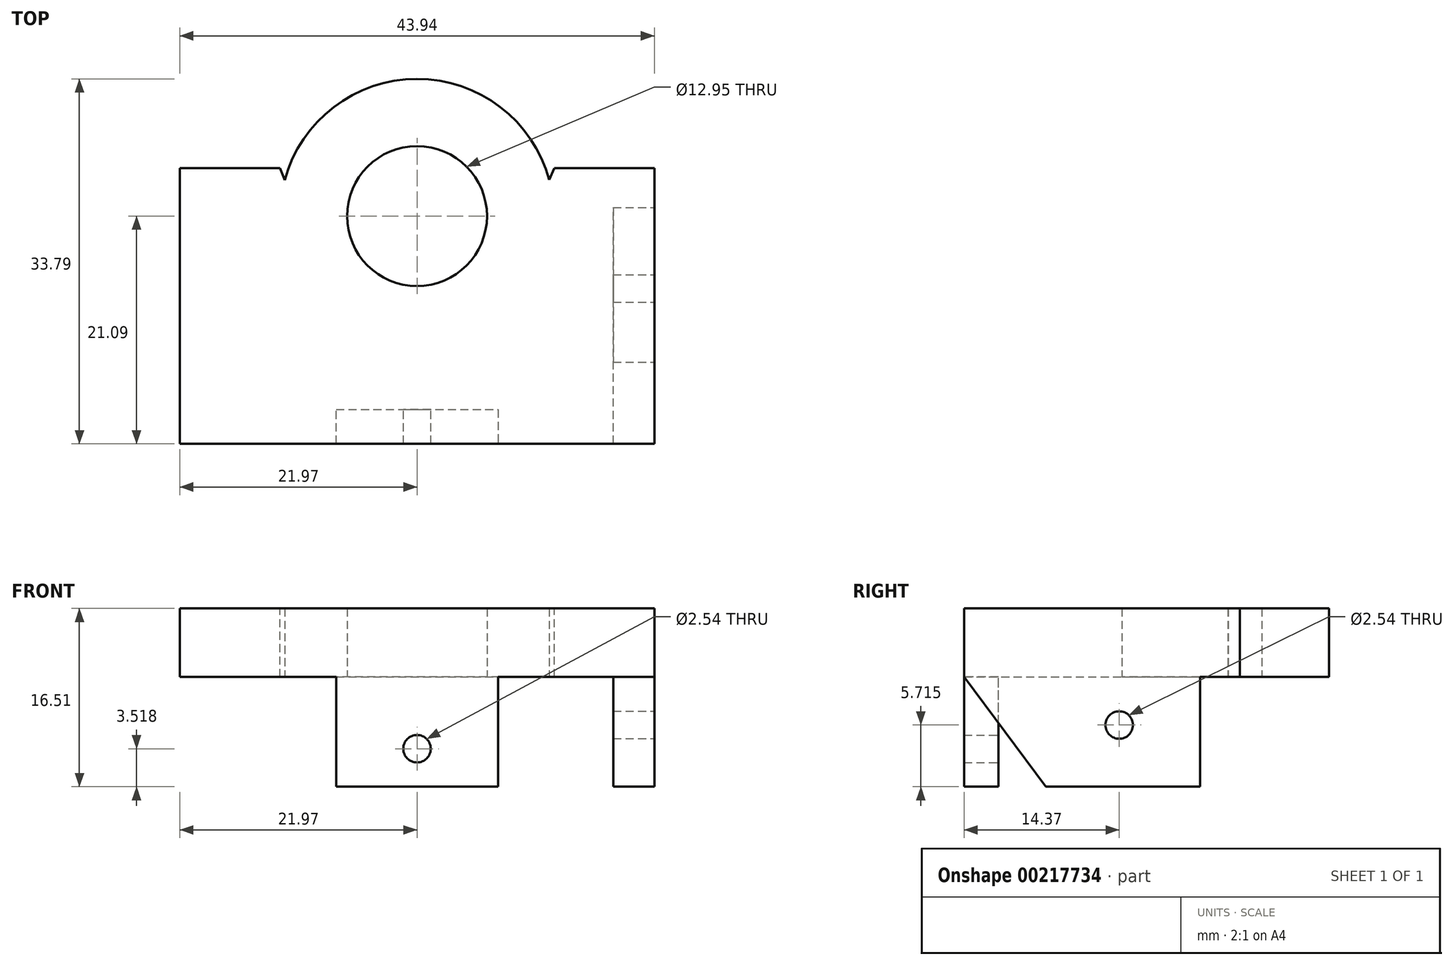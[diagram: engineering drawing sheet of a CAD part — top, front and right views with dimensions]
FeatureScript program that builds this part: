
annotation { "Feature Type Name" : "Feature", "Feature Type Description" : "" }
export const myFeature = defineFeature(function(context is Context, id is Id, definition is map)
    precondition{}
    {
        {
            var Q0;
            Q0=qCreatedBy(makeId("Top.planeOp"),FACE);
            var sketch = newSketch(context, id + "F0", { "sketchPlane" : qUnion([Q0])});
            skCircle(sketch, "E0", {"center": v(0, 0) * mm, "radius": 6.48 * mm});
            skCircle(sketch, "E1", {"center": v(0, 0) * mm, "radius": 12.7 * mm});
            skSolve(sketch);
        }
        {
            var Q0;
            Q0=qSketchRegion(id+"F0",true);
            extrude(context, id + "F1", {"entities" : qUnion([Q0]), "depth" : 6.35 * mm});
        }
        {
            var Q0;
            Q0=makeQuery(id+"F1.opExtrude","CAP_FACE",FACE,{"disambiguationData":[OSD([sQuery(id+"F0.wireOp",EDGE,"E0"),sQuery(id+"F0.wireOp",EDGE,"E1")])],"isStart":false});
            var sketch = newSketch(context, id + "F2", { "sketchPlane" : qUnion([Q0])});
            skLineSegment(sketch, "E2", {"start": v(0, -21.09) * mm, "end": v(-21.97, -21.09) * mm});
            skLineSegment(sketch, "E3", {"start": v(0, -21.09) * mm, "end": v(21.97, -21.09) * mm});
            skLineSegment(sketch, "E4", {"start": v(21.97, -21.09) * mm, "end": v(21.97, -17.91) * mm});
            skLineSegment(sketch, "E5", {"start": v(-21.97, -21.09) * mm, "end": v(-21.97, -17.9) * mm});
            skLineSegment(sketch, "E6", {"start": v(21.97, -17.91) * mm, "end": v(21.97, 4.45) * mm});
            skLineSegment(sketch, "E7", {"start": v(21.97, 4.45) * mm, "end": v(12.7, 4.45) * mm});
            skLineSegment(sketch, "E8", {"start": v(-21.97, -17.9) * mm, "end": v(-21.97, 4.45) * mm});
            skLineSegment(sketch, "E9", {"start": v(-21.97, 4.45) * mm, "end": v(-12.7, 4.45) * mm});
            skLineSegment(sketch, "E10", {"start": v(-12.7, 4.45) * mm, "end": v(-6.95, -9.77) * mm});
            skLineSegment(sketch, "E11", {"start": v(-6.95, -9.77) * mm, "end": v(6.77, -9.77) * mm});
            skLineSegment(sketch, "E12", {"start": v(6.77, -9.77) * mm, "end": v(12.7, 4.45) * mm});
            skSolve(sketch);
        }
        {
            var Q0;
            Q0=qSketchRegion(id+"F2",true);
            extrude(context, id + "F3", {"entities" : qUnion([Q0]), "operationType" : NewBodyOperationType.ADD, "oppositeDirection" : true, "depth" : 6.35 * mm});
        }
        {
            var Q0;
            Q0=makeQuery(id+"F3.opExtrude","SWEPT_FACE",FACE,{"disambiguationData":[OSD([sQuery(id+"F2.wireOp",EDGE,"E4")])]});
            var sketch = newSketch(context, id + "F4", { "sketchPlane" : qUnion([Q0])});
            skLineSegment(sketch, "E13", {"start": v(-21.09, 6.35) * mm, "end": v(0.78, 6.35) * mm});
            skLineSegment(sketch, "E14", {"start": v(0.78, 6.35) * mm, "end": v(0.78, -10.16) * mm});
            skLineSegment(sketch, "E15", {"start": v(0.78, -10.16) * mm, "end": v(-13.53, -10.16) * mm});
            skLineSegment(sketch, "E16", {"start": v(-21.09, 0) * mm, "end": v(-21.09, 6.35) * mm});
            skLineSegment(sketch, "E17", {"start": v(0.78, -10.16) * mm, "end": v(-6.72, -10.16) * mm});
            skLineSegment(sketch, "E18", {"start": v(-6.72, -10.16) * mm, "end": v(-6.72, -4.45) * mm});
            skPoint(sketch, "E18.endSnap0", {"position": v(0.78, -1.9) * mm});
            skCircle(sketch, "E19", {"center": v(-6.72, -4.45) * mm, "radius": 1.27 * mm});
            skLineSegment(sketch, "E20", {"start": v(-21.09, 0) * mm, "end": v(-13.53, -10.16) * mm});
            skPoint(sketch, "E21.orphan", {"position": v(-21.09, -10.16) * mm});
            skPoint(sketch, "E22.orphan", {"position": v(-6.72, -1.9) * mm});
            skSolve(sketch);
        }
        {
            var Q0;
            Q0 = qSketchRegion(id + "F4", true);
            extrude(context, id + "F5", {"entities" : qUnion([Q0]), "operationType" : NewBodyOperationType.ADD, "oppositeDirection" : true, "depth" : 3.8 * mm});
        }
        {
            var Q0;
            Q0=makeQuery(id+"F3.boolean.opBoolean","MERGE",FACE,{"derivedFrom":[makeQuery(id+"F1.opExtrude","CAP_FACE",FACE,{"disambiguationData":[OSD([sQuery(id+"F0.wireOp",EDGE,"E0"),sQuery(id+"F0.wireOp",EDGE,"E1")])],"isStart":true}),makeQuery(id+"F3.opExtrude","CAP_FACE",FACE,{"disambiguationData":[OSD([sQuery(id+"F2.wireOp",EDGE,"E2"),sQuery(id+"F2.wireOp",EDGE,"E3"),sQuery(id+"F2.wireOp",EDGE,"E4"),sQuery(id+"F2.wireOp",EDGE,"E5"),sQuery(id+"F2.wireOp",EDGE,"ihHadCWb-XjeW-R3a0-dGNE-DLv68DcTVQ7N"),sQuery(id+"F2.wireOp",EDGE,"1IoPUFMC-zjit-IGW3-BYE7-LK0CDHMM8rKh"),sQuery(id+"F2.wireOp",EDGE,"NdcEkIWE-Nxbb-I5WJ-c0X4-1hDUIVkZ8ckX"),sQuery(id+"F2.wireOp",EDGE,"YiZrzofx-tHcN-ggQp-RaR3-rrEU8t4WHX24"),sQuery(id+"F2.wireOp",EDGE,"RK1YeRvc-nPOg-Eqkx-etu6-UXfsHSOCRuCc"),sQuery(id+"F2.wireOp",EDGE,"3zleHhUL-0sEu-ddFR-184l-ClsJvtk2H4PM")])],"isStart":false})]});
            var sketch = newSketch(context, id + "F6", { "sketchPlane" : qUnion([Q0])});
            skLineSegment(sketch, "E23", {"start": v(0, 21.09) * mm, "end": v(7.5, 21.09) * mm});
            skLineSegment(sketch, "E24", {"start": v(0, 21.09) * mm, "end": v(-7.5, 21.09) * mm});
            skLineSegment(sketch, "E25", {"start": v(-7.5, 21.09) * mm, "end": v(-7.5, 17.91) * mm});
            skLineSegment(sketch, "E26", {"start": v(-7.5, 17.91) * mm, "end": v(7.5, 17.91) * mm});
            skLineSegment(sketch, "E27", {"start": v(7.5, 17.91) * mm, "end": v(7.5, 21.09) * mm});
            skSolve(sketch);
        }
        {
            var Q0;
            Q0 = qSketchRegion(id + "F6", true);
            extrude(context, id + "F7", {"entities" : qUnion([Q0]), "operationType" : NewBodyOperationType.ADD, "depth" : 10.16 * mm});
        }
        {
            var Q0;
            Q0=makeQuery(id+"F7.opExtrude","SWEPT_FACE",FACE,{"disambiguationData":[OSD([sQuery(id+"F6.wireOp",EDGE,"E26")])]});
            var sketch = newSketch(context, id + "F8", { "sketchPlane" : qUnion([Q0])});
            skLineSegment(sketch, "E28", {"start": v(0, -10.16) * mm, "end": v(0, -6.64) * mm});
            skPoint(sketch, "E28.endSnap0", {"position": v(0, -10.16) * mm});
            skCircle(sketch, "E29", {"center": v(0, -6.64) * mm, "radius": 1.27 * mm});
            skSolve(sketch);
        }
        {
            var Q0;
            Q0 = qSketchRegion(id + "F8", true);
            extrude(context, id + "F9", {"entities" : qUnion([Q0]), "operationType" : NewBodyOperationType.REMOVE, "oppositeDirection" : true, "depth" : 25.4 * mm});
        }
    });
